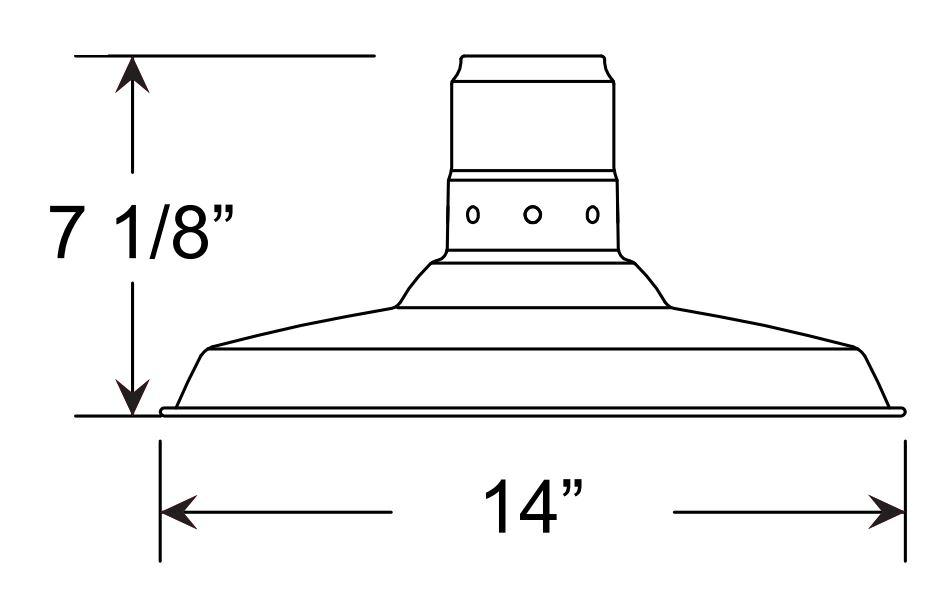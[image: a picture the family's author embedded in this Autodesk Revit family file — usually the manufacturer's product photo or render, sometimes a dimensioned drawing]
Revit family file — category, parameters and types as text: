
# Revit family: OSSD 20,24,36,42 MB
name_source: partatom
category: Lighting Fixtures
units: mm (PartAtom-declared; Revit-internal decimal feet)

## family parameters
Always vertical = Yes
Cut with Voids When Loaded = No
Light Source = Yes
OmniClass Number = 23.80.70.00
OmniClass Title = Lighting
Part Type = Normal
Room Calculation Point = No
Round Connector Dimension = Use Diameter
Shared = No
Work Plane-Based = No

## types (4) — shared parameters
Apparent Load = 200 VA
Body Colour = Spun aluminium
Body Material = body
Bulb = BULB
CRI = >90
Canopy Body = body
Color Filter = 16777215
Construction Material = Heavy Duty spun aluminum.
Default Elevation = 0' - 0"
Description = 120-277 Voltage
Dimming = 1%
Dimming Lamp Color Temperature Shift = <None>
Efficiency = 65-125 lumens per watt
INSIDE BODY = Default
Lamp = MB
Life = L70 50,000 hours
Load Classification = Lighting
Manufacturer = ANP Lighting
Power Factor = 1
Tilt Angle = 90.00°
URL = https://www.anplighting.com
Voltage = 277 V
Warranty = 5 year limited warranty
Wattage Comments = 200 W MAX
b = 0' - 2"

## per-type parameters (varying)
| type | Fixture Diameter | Fixture Height | OSSD24 | OSSD30 | OSSD36 | OSSD42 | Photometric Web File | Weight | a |
| OSSD24 | 2' - 0" | 1' - 0" | Yes | No | No | No | OSSD30M037LDDW35K.ies | 10.0 lbs | 0' - 10" |
| OSSD30 | 2' - 0" | 1' - 0" | No | Yes | No | No | OSSD30M037LDDW35K.ies | 13.0 lbs | 0' - 11" |
| OSSD36 | 3' - 0" | 1' - 6" | No | No | Yes | No | OSSD36M037LDDW35K.ies | 18.0 lbs | 0' - 10" |
| OSSD42 | 3' - 6" | 1' - 9" | No | No | No | Yes | OSSD42M037LDDW35K.ies | 23.5lbs | 0' - 10" |

note: column(s) folded — value = type name in every type: Model

## geometry (parser evidence)
native form markers: Sweep x38
no freeform markers — native parametric forms only
